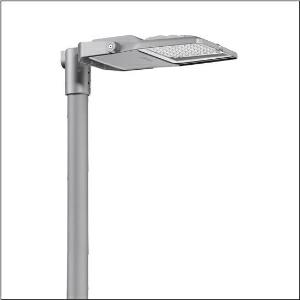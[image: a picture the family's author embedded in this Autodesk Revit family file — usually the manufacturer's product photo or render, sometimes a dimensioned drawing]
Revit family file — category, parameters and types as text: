
# Revit family: floodlight_fl_21_iq_mini___pl64_5xa7772b2e3a_76f3
name_source: partatom
category: Lighting Fixtures
units: mm (PartAtom-declared; Revit-internal decimal feet)

## family parameters
Cut with Voids When Loaded = No
Host = Face
Light Source = No
Part Type = Normal
Room Calculation Point = No
Round Connector Dimension = Use Diameter
Shared = No

## types (1)
- --- (1 x LED, 6020 lm, 45.5 W, 3000K)
    Apparent Load = 46 VA
    CIE Flux Codes = 28 80 98 100 100
    Color Rendering = 70
    Color Temperature = 3000K
    Default Elevation = 1800 mm
    Description = Floodlight FL 21 iQ mini, floodlight, primary light control with lens, of PMMA, primary optical cover: protective disc, of toughened safety glass, transparent, light distribution: PL64, light emission: direct distribution, installation type: surface-mounted, LED, High Power LED, rated luminous flux: 6.020lm, luminous efficacy: 132lm/W, light colour: 730, colour temperature: 3000K, control: Auto-Match, Temp-Guard, Night-Set, Smart-Wire, Desk-Remote (wireless, voltage-free reading and setting of iQ features in the workshop via application-optimized NFC function/RFID function), optimised constant luminous flux control (CLO 2.0), Light-Fading, Lumen-Switch, with terminal, 6-pole, mains connection: 220..240V, AC, 50/60Hz, start of lifetime: 46W, end of service life: 48W, reduction: 22W, luminaire housing, of diecast aluminium, powder-coated, Siteco® metallic grey (DB 702S), corrosivity category C5 mid according to DIN EN ISO 12944, sealing non-destructively replaceable, please order mast flange separately, mast bracket, of steel, galvanised, powder-coated, protection rating (complete): IP66, insulation class (complete): insulation class II (safety insulation), certification: CE, ENEC, VDE, protection symbol: D, impact resistance: IK08, permissible operating ambient temperature: -40..+40°C, permissible operating ambient temperature for outdoor applications: -40..+50°C, standard: DIN EN 12944, LABS conformity tested according to VDMA 24364:2018-05, packaging unit: 1 piece

Light Distribution: PL64
    Height = 70 mm
    Lamp = 1 x LED
    Lamp Light Flux = 6020 lm
    Lamp Power = 45.5 W
    Lamp count = 1
    Length = 485 mm
    Luminous efficacy = 132 lm/W
    Manufacturer = Siteco
    ModVariant = No
    Model = 5XA7772B2E3A
    Number of Poles = 1
    OnlyDefault = Yes
    Power Factor = 1
    Product Name = Floodlight FL 21 iQ mini | PL64
    Product group = floodlight | pylon annexe
    ProductGroupID = 6200
    Protection Class = Protection class II
    Protection Degree = IP 66
    RLX_Detail_Level = 1
    RLX_Emergency_Light_Flux = 0 lm
    RLX_Emergency_Type = 0
    RLX_Emergency_Type_DB = No
    RlxData = <blob elided: 101229 chars, md5=42bead31>
    Socket = socket
    Standby Power = 0 W
    System Light Flux = 6020 lm
    System Power = 46 W
    Type Comments = factory setting: luminous flux: 100 % | dim-lin: 254 | 463 mA
    Type Image = l_1007125.jpg
    URL = http://relux.com
    VarID = @adj_137235
    Voltage = 0 V
    Weight = 0.00 kg
    Width = 337 mm

## geometry (parser evidence)
native form markers: Blend x4, Sweep x12
no freeform markers — native parametric forms only
